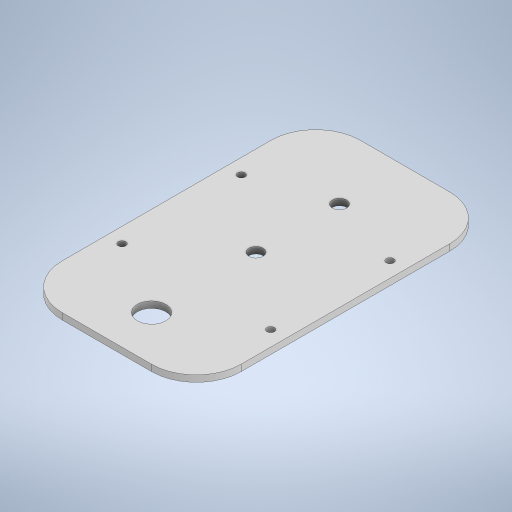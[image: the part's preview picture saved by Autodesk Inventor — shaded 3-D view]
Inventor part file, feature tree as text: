
AUTODESK INVENTOR PART (.ipt)
format: ipt  version: 2024 (Build 280153000, 153)  size: 263,680 bytes
history: native  units: mm
features: extrude x4, fillet x1
ambient origin geometry x8: Origin, YZ Plane, XZ Plane, XY Plane, X Axis, Y Axis, Z Axis, Center Point
bodies: Solid1 (feature_tree)
feature tree (5):
  extrude  "Extrusion1"  Depth=150.0mm
  fillet  "Fillet1"  Radius=250.0mm
  extrude  "Extrusion2"  Depth=5.4mm TaperAngle=0.0deg
  extrude  "Extrusion3"  Depth=37.5mm
  extrude  "Extrusion4"  Depth=75.0mm
